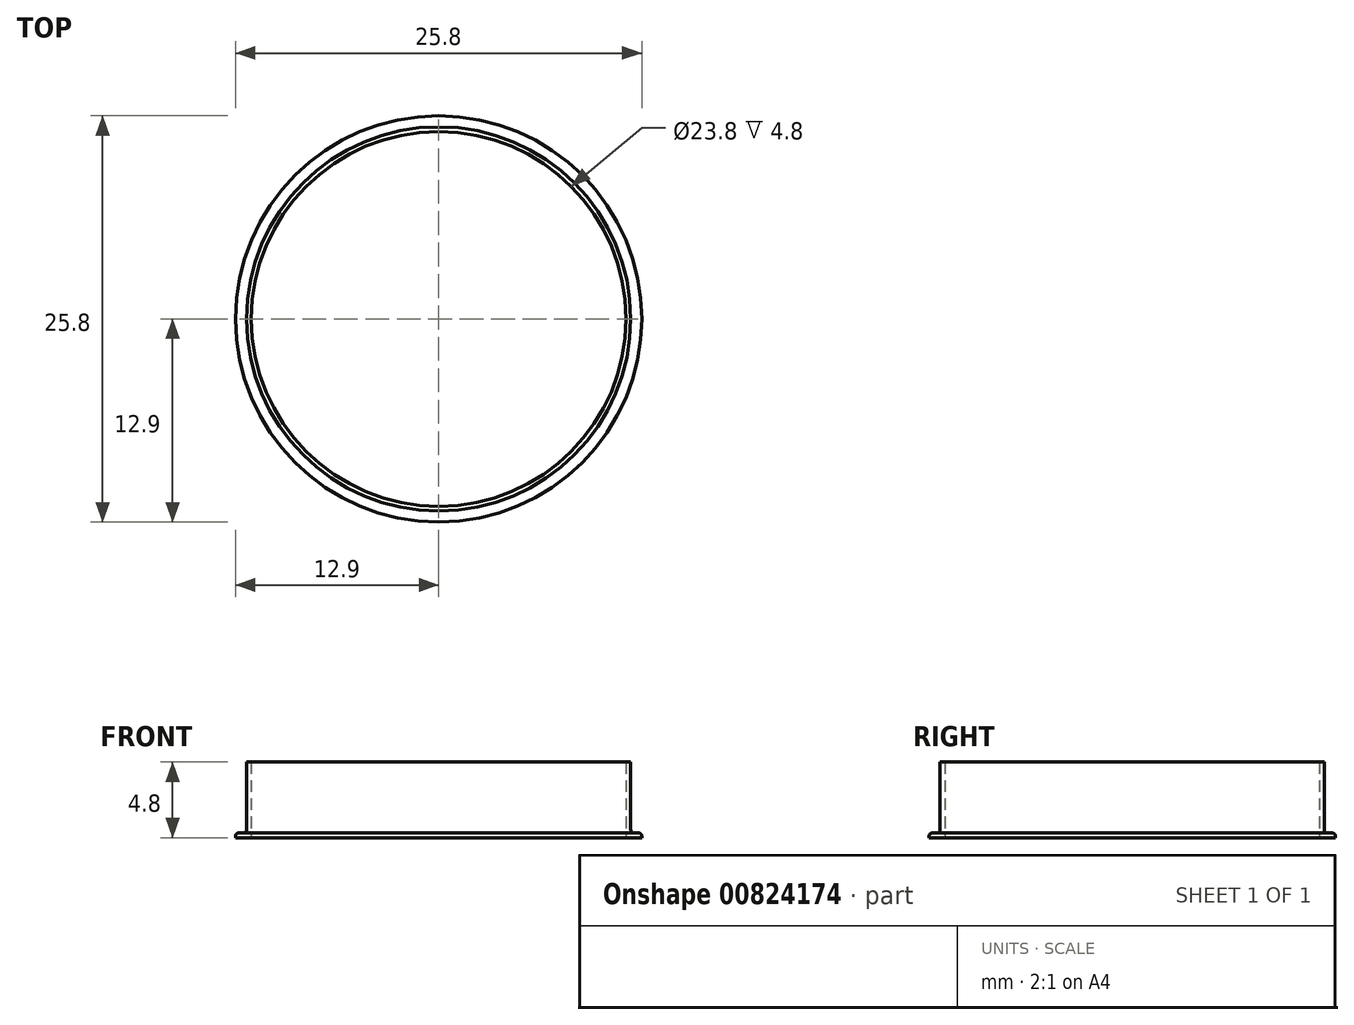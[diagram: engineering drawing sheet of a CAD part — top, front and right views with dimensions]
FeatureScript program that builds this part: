
annotation { "Feature Type Name" : "Feature", "Feature Type Description" : "" }
export const myFeature = defineFeature(function(context is Context, id is Id, definition is map)
    precondition{}
    {
        {
            var Q0;
            Q0=qCreatedBy(makeId("Front.planeOp"),FACE);
            var sketch = newSketch(context, id + "F0", { "sketchPlane" : qUnion([Q0])});
            skLineSegment(sketch, "E0", {"start": v(0, 0) * mm, "end": v(0, 4.8) * mm, "construction": true});
            skLineSegment(sketch, "E1", {"start": v(0, 0) * mm, "end": v(11.9, 0) * mm, "construction": true});
            skLineSegment(sketch, "E2", {"start": v(11.9, 0) * mm, "end": v(11.9, 4.8) * mm});
            skLineSegment(sketch, "E3", {"start": v(11.9, 0) * mm, "end": v(12.9, 0) * mm});
            skLineSegment(sketch, "E4.0", {"start": v(12.2, 0.3) * mm, "end": v(12.2, 4.8) * mm});
            skLineSegment(sketch, "E5.0", {"start": v(12.2, 0.3) * mm, "end": v(12.9, 0.3) * mm});
            skLineSegment(sketch, "E6", {"start": v(12.9, 0.3) * mm, "end": v(12.9, 0) * mm});
            skLineSegment(sketch, "E7", {"start": v(11.9, 4.8) * mm, "end": v(12.2, 4.8) * mm});
            skSolve(sketch);
        }
        {
            var Q0;
            Q0=qCreatedBy(makeId("Front.planeOp"),FACE);
            var sketch = newSketch(context, id + "F1", { "sketchPlane" : qUnion([Q0])});
            skLineSegment(sketch, "E8", {"start": v(0, 0) * mm, "end": v(0, 6.2) * mm});
            skSolve(sketch);
        }
        {
            var Q0;
            Q0=makeQuery(id+"F0.imprint","IMPRINT",FACE,{"disambiguationData":[TD([[makeQuery(id+"F0.imprint","IMPRINT",EDGE,{"derivedFrom":sQuery(id+"F0.wireOp",EDGE,"E2")}),-1.0]])]});
            var Q1;
            Q1=sQuery(id+"F1.wireOp",EDGE,"E8");
            revolve(context, id + "F2", {"surfaceOperationType" : NewSurfaceOperationType.NEW, "entities" : qUnion([Q0]), "axis" : qUnion([Q1]), "revolveType" : RevolveType.FULL});
        }
        {
            var Q0;
            Q0=makeQuery(id+"F2.opRevolve","SWEPT_EDGE",EDGE,{"disambiguationData":[OSD([sQuery(id+"F0.wireOp",EDGE,"E4.0"),sQuery(id+"F0.wireOp",EDGE,"E5.0")])]});
            fillet(context, id + "F3", {"entities" : qUnion([Q0]), "radius" : .2 * mm, "tangentPropagation" : true, "allowEdgeOverflow" : false});
        }
        {
            var Q0;
            Q0=makeQuery(id+"F2.opRevolve","SWEPT_EDGE",EDGE,{"disambiguationData":[OSD([sQuery(id+"F0.wireOp",EDGE,"E5.0"),sQuery(id+"F0.wireOp",EDGE,"E6")])]});
            fillet(context, id + "F4", {"entities" : qUnion([Q0]), "radius" : 0.2 * mm, "tangentPropagation" : true, "allowEdgeOverflow" : false});
        }
    });
